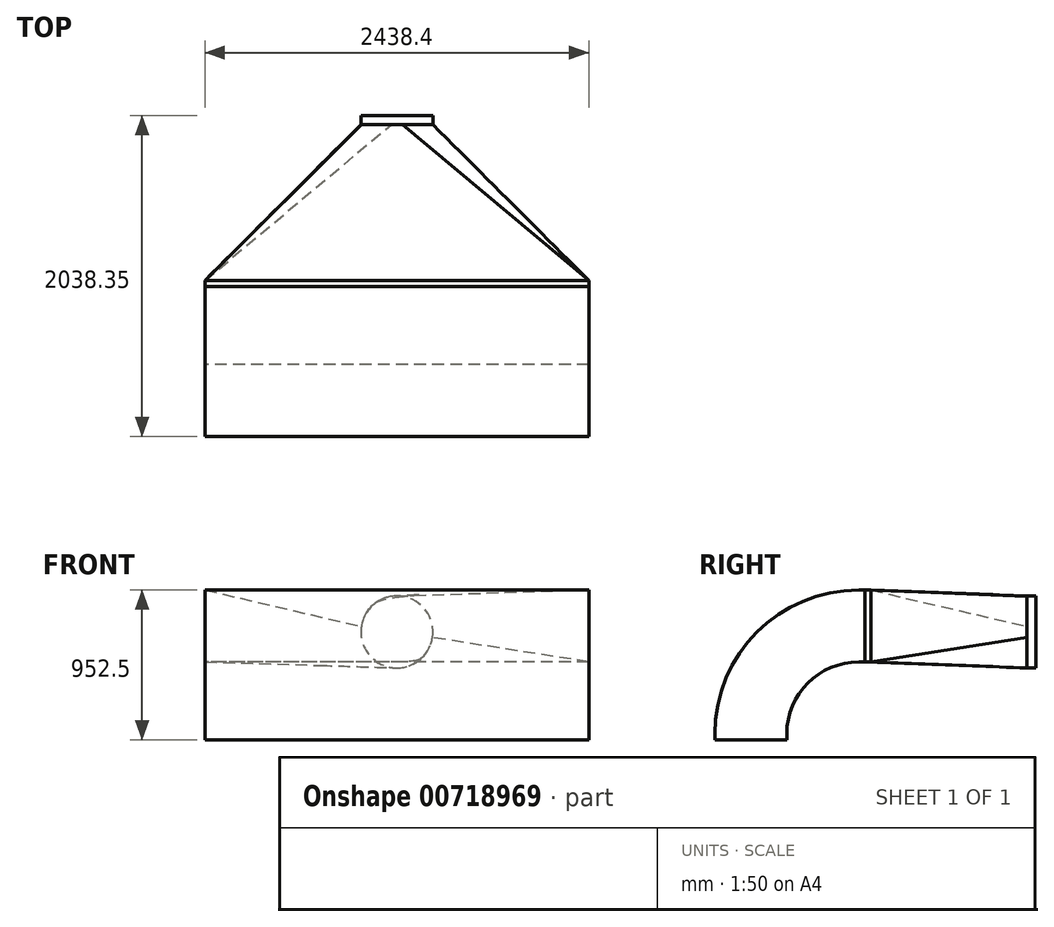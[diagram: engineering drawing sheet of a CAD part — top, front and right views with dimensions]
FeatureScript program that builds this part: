
annotation { "Feature Type Name" : "Feature", "Feature Type Description" : "" }
export const myFeature = defineFeature(function(context is Context, id is Id, definition is map)
    precondition{}
    {
        {
            var Q0;
            Q0=qCreatedBy(makeId("Top.planeOp"),FACE);
            var sketch = newSketch(context, id + "F0", { "sketchPlane" : qUnion([Q0])});
            skLineSegment(sketch, "E0.bottom", {"start": v(1219.2, 228.6) * mm, "end": v(-1219.2, 228.6) * mm});
            skLineSegment(sketch, "E0.top", {"start": v(1219.2, -228.6) * mm, "end": v(-1219.2, -228.6) * mm});
            skLineSegment(sketch, "E0.left", {"start": v(1219.2, 228.6) * mm, "end": v(1219.2, -228.6) * mm});
            skLineSegment(sketch, "E0.right", {"start": v(-1219.2, 228.6) * mm, "end": v(-1219.2, -228.6) * mm});
            skPoint(sketch, "E0.middle", {"position": v(0, 0) * mm});
            skSolve(sketch);
        }
        {
            var Q0;
            Q0=makeQuery(id+"F0.imprint","IMPRINT",FACE,{"disambiguationData":[TD([[makeQuery(id+"F0.imprint","IMPRINT",EDGE,{"derivedFrom":sQuery(id+"F0.wireOp",EDGE,"E0.bottom")}),1.0]])]});
            extrude(context, id + "F1", {"entities" : qUnion([Q0]), "depth" : 38.1 * mm, "offsetDistance" : 25.4 * mm});
        }
        {
            var Q0;
            Q0=makeQuery(id+"F1.opExtrude","CAP_FACE",FACE,{"disambiguationData":[OSD([sQuery(id+"F0.wireOp",EDGE,"E0.bottom"),sQuery(id+"F0.wireOp",EDGE,"E0.top"),sQuery(id+"F0.wireOp",EDGE,"E0.left"),sQuery(id+"F0.wireOp",EDGE,"E0.right")])],"isStart":false});
            var sketch = newSketch(context, id + "F2", { "sketchPlane" : qUnion([Q0])});
            skLineSegment(sketch, "E1", {"start": v(0, 0) * mm, "end": v(0, 685.8) * mm, "construction": true});
            skPoint(sketch, "E1.endSnap0", {"position": v(0, 228.6) * mm});
            skLineSegment(sketch, "E2", {"start": v(0, 685.8) * mm, "end": v(-206.41, 685.8) * mm});
            skSolve(sketch);
        }
        {
            var Q0;
            Q0=makeQuery(id+"F2.imprint","IMPRINT",FACE,{"disambiguationData":[TD([[makeQuery(id+"F2.imprint","IMPRINT",EDGE,{"derivedFrom":makeQuery(id+"F1.opExtrude","CAP_EDGE",EDGE,{"disambiguationData":[OSD([sQuery(id+"F0.wireOp",EDGE,"E0.bottom")])],"isStart":false})}),1.0]])]});
            var Q1;
            Q1=sQuery(id+"F2.wireOp",EDGE,"E2");
            revolve(context, id + "F3", {"operationType" : NewBodyOperationType.ADD, "surfaceOperationType" : NewSurfaceOperationType.NEW, "entities" : qUnion([Q0]), "axis" : qUnion([Q1]), "revolveType" : RevolveType.ONE_DIRECTION, "angle" : 90 * degree});
        }
        {
            var Q0;
            Q0=makeQuery(id+"F3.opRevolve","CAP_FACE",FACE,{"disambiguationData":[OSD([sQuery(id+"F0.wireOp",EDGE,"E0.bottom"),sQuery(id+"F0.wireOp",EDGE,"E0.top"),sQuery(id+"F0.wireOp",EDGE,"E0.left"),sQuery(id+"F0.wireOp",EDGE,"E0.right")])],"isStart":false});
            extrude(context, id + "F4", {"entities" : qUnion([Q0]), "operationType" : NewBodyOperationType.ADD, "depth" : 38.1 * mm, "offsetDistance" : 25.4 * mm});
        }
        {
            var Q0;
            Q0=makeQuery(id+"F4.opExtrude","CAP_FACE",FACE,{"disambiguationData":[OSD([sQuery(id+"F0.wireOp",EDGE,"E0.bottom"),sQuery(id+"F0.wireOp",EDGE,"E0.top"),sQuery(id+"F0.wireOp",EDGE,"E0.left"),sQuery(id+"F0.wireOp",EDGE,"E0.right")])],"isStart":false});
            var sketch = newSketch(context, id + "F5", { "sketchPlane" : qUnion([Q0])});
            skLineSegment(sketch, "E3.bottom", {"start": v(-1219.2, 952.5) * mm, "end": v(1219.2, 952.5) * mm});
            skLineSegment(sketch, "E3.top", {"start": v(-1219.2, 495.3) * mm, "end": v(1219.2, 495.3) * mm});
            skLineSegment(sketch, "E3.left", {"start": v(-1219.2, 952.5) * mm, "end": v(-1219.2, 495.3) * mm});
            skLineSegment(sketch, "E3.right", {"start": v(1219.2, 952.5) * mm, "end": v(1219.2, 495.3) * mm});
            skSolve(sketch);
        }
        {
            var Q0;
            Q0=qSketchRegion(id+"F5",true);
            extrude(context, id + "F6", {"entities" : qUnion([Q0]), "depth" : 38.1 * mm, "offsetDistance" : 25.4 * mm});
        }
        {
            var Q0;
            Q0=makeQuery(id+"F6.opExtrude","CAP_FACE",FACE,{"disambiguationData":[OSD([sQuery(id+"F5.wireOp",EDGE,"E3.bottom"),sQuery(id+"F5.wireOp",EDGE,"E3.top"),sQuery(id+"F5.wireOp",EDGE,"E3.left"),sQuery(id+"F5.wireOp",EDGE,"E3.right")])],"isStart":false});
            cPlane(context, id + "F7", {"entities" : qUnion([Q0]), "cplaneType" : CPlaneType.OFFSET, "offset" : 990.6 * mm, "width" : 152.4 * mm, "height" : 152.4 * mm});
        }
        {
            var Q0;
            Q0=qCreatedBy(id+"F7.planeOp",FACE);
            var sketch = newSketch(context, id + "F8", { "sketchPlane" : qUnion([Q0])});
            skLineSegment(sketch, "E4", {"start": v(0, 0) * mm, "end": v(0, 685.8) * mm, "construction": true});
            skCircle(sketch, "E5", {"center": v(0, 685.8) * mm, "radius": 228.6 * mm});
            skSolve(sketch);
        }
        {
            var Q1;
            Q1=makeQuery(id+"F6.opExtrude","CAP_FACE",FACE,{"disambiguationData":[OSD([sQuery(id+"F5.wireOp",EDGE,"E3.bottom"),sQuery(id+"F5.wireOp",EDGE,"E3.top"),sQuery(id+"F5.wireOp",EDGE,"E3.left"),sQuery(id+"F5.wireOp",EDGE,"E3.right")])],"isStart":false});
            var Q2;
            Q2=makeQuery(id+"F8.imprint","IMPRINT",FACE,{"disambiguationData":[TD([[makeQuery(id+"F8.imprint","IMPRINT",EDGE,{"derivedFrom":sQuery(id+"F8.wireOp",EDGE,"E5")}),1.0]])]});
            loft(context, id + "F9", {"operationType" : NewBodyOperationType.ADD, "sheetProfilesArray" : [{ "sheetProfileEntities" : qUnion([Q1]) }, { "sheetProfileEntities" : qUnion([Q2]) }]});
        }
        {
            var Q0;
            Q0=makeQuery(id+"F9.opLoft","CAP_FACE",FACE,{"disambiguationData":[OSD([makeQuery(id+"F8.imprint","IMPRINT",FACE,{"disambiguationData":[TD([[makeQuery(id+"F8.imprint","IMPRINT",EDGE,{"derivedFrom":sQuery(id+"F8.wireOp",EDGE,"E5")}),1.0]])]})])],"isStart":true});
            extrude(context, id + "F10", {"entities" : qUnion([Q0]), "operationType" : NewBodyOperationType.ADD, "depth" : 57.15 * mm, "offsetDistance" : 25.4 * mm});
        }
    });
